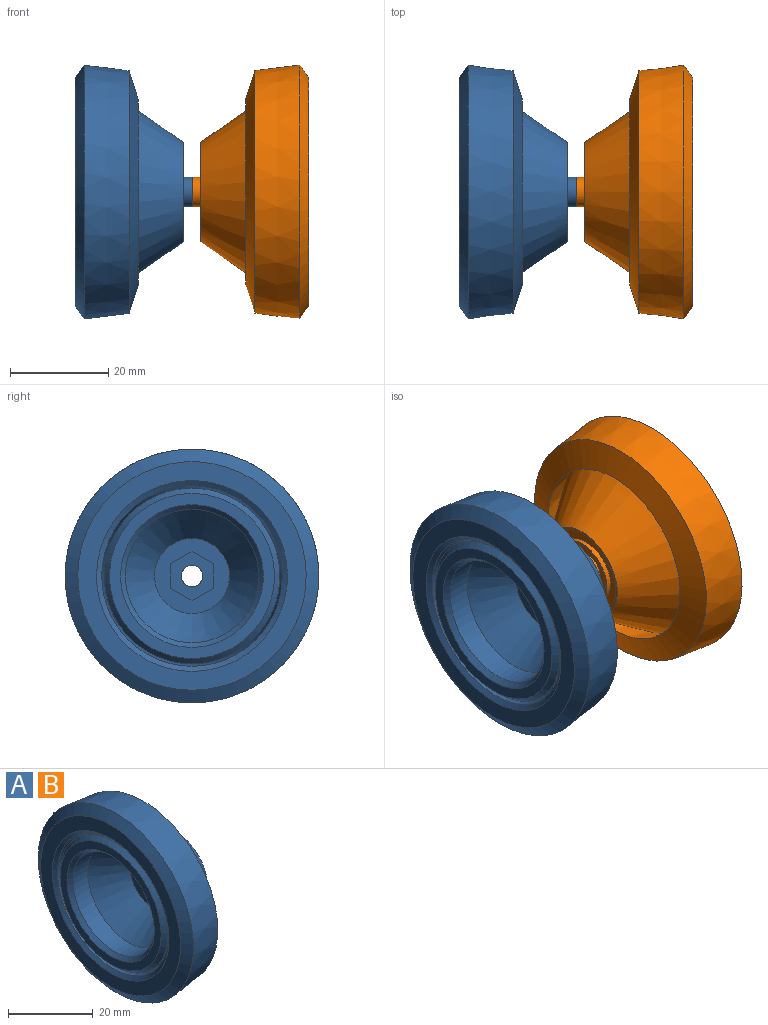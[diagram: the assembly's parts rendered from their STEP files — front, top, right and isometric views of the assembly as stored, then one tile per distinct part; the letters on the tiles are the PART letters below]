
ASSEMBLY  parts=2 mates=1
PART A: 35 faces, bbox 23.8x51.7x51.7 mm
  f0: cylinder r=2.2mm len=6.62mm, axis (1,0,0), area 91.4mm2, adj f24,f34
  f1: cylinder r=3.8mm len=7.6mm, axis (1,0,0), area 26.9mm2, adj f2,f26
  f2: plane 13.3x13.3mm, normal (1,0,0), area 93.6mm2, adj f1,f3
  f3: cylinder r=6.65mm len=13.3mm, axis (1,0,0), area 62.7mm2, adj f2,f4
  f4: plane 14.3x14.3mm, normal (1,0,0), area 21.7mm2, adj f3,f5
  f5: cylinder r=7.15mm len=14.3mm, axis (1,0,0), area 48.3mm2, adj f4,f6
  f6: plane 19.3x19.3mm, normal (1,0,0), area 131.9mm2, adj f5,f7
  f7: cylinder r=9.65mm len=19.3mm, axis (1,0,0), area 65.2mm2, adj f6,f8
  f8: plane 20.3x20.3mm, normal (1,0,0), area 31.1mm2, adj f7,f9
  f9: cone r=20.12mm half-angle=34.6deg, axis (-1,0,0), area 1670.5mm2, adj f8,f10
  f10: cone r=18.98mm half-angle=12.3deg, axis (-1,0,0), area 656.5mm2, adj f9,f11
  f11: cone r=24.74mm half-angle=72.3deg, axis (-1,0,0), area 830.5mm2, adj f10,f12
  f12: cone r=25.86mm half-angle=6.9deg, axis (-1,0,0), area 1467.2mm2, adj f11,f13
  f13: cone r=25.86mm half-angle=55.8deg, axis (1,0,0), area 481.6mm2, adj f12,f14
  f14: plane 46.55x46.55mm, normal (-1,0,0), area 514.2mm2, adj f13,f15
  f15: cone r=18.39mm half-angle=55.8deg, axis (-1,0,0), area 151.5mm2, adj f14,f16
  f16: cone r=18.39mm half-angle=8.7deg, axis (-1,0,0), area 367.7mm2, adj f15,f17
  f17: cylinder r=17.91mm len=35.81mm, axis (1,0,0), area 304mm2, adj f16,f18
  f18: cone r=17.91mm half-angle=42.3deg, axis (1,0,0), area 177.5mm2, adj f17,f19
  f19: plane 33.62x33.62mm, normal (-1,0,0), area 223.2mm2, adj f18,f20
  f20: cone r=14.54mm half-angle=42.2deg, axis (-1,0,0), area 126mm2, adj f19,f21
  f21: cylinder r=13.59mm len=27.17mm, axis (1,0,0), area 417.6mm2, adj f20,f22
  f22: cone r=13.59mm half-angle=36deg, axis (-1,0,0), area 674.8mm2, adj f21,f23
  f23: plane 15.28x15.28mm, normal (-1,0,0), area 118.5mm2, adj f22,f28,f29,f30,f31,f32,f33
  f24: plane 6x6mm, normal (1,0,0), area 13.1mm2, adj f0,f25
  f25: cylinder r=3mm len=6mm, axis (1,0,0), area 36.3mm2, adj f24,f27
  f26: plane 7.6x7.6mm, normal (1,0,0), area 13.2mm2, adj f1,f27
  f27: cone r=3mm half-angle=45deg, axis (-1,0,0), area 5.5mm2, adj f25,f26
  f28: plane 5x3mm, normal (0,1,0), area 15mm2, adj f23,f29,f33,f34
  f29: plane 4.33x3mm, normal (0,0.5,-0.87), area 15mm2, adj f23,f28,f30,f34
  f30: plane 4.33x3mm, normal (0,-0.5,-0.87), area 15mm2, adj f23,f29,f31,f34
  f31: plane 5x3mm, normal (0,-1,0), area 15mm2, adj f23,f30,f32,f34
  f32: plane 4.33x3mm, normal (0,-0.5,0.87), area 15mm2, adj f23,f31,f33,f34
  f33: plane 4.33x3mm, normal (0,0.5,0.87), area 15mm2, adj f23,f28,f32,f34
  f34: plane 10x8.66mm, normal (-1,0,0), area 49.7mm2, adj f0,f28,f29,f30,f31,f32,f33
PART B: same geometry as A
PLACE A t=(-10.75,-0.73,-22.86)mm
PLACE B rot(axis=(0,1,0),180deg) t=(-9.25,-0.73,-22.86)mm
MATE fastened B.f0 <-> A.f0  axis (-1,0,0) through (-10,-0.73,-22.86)mm
